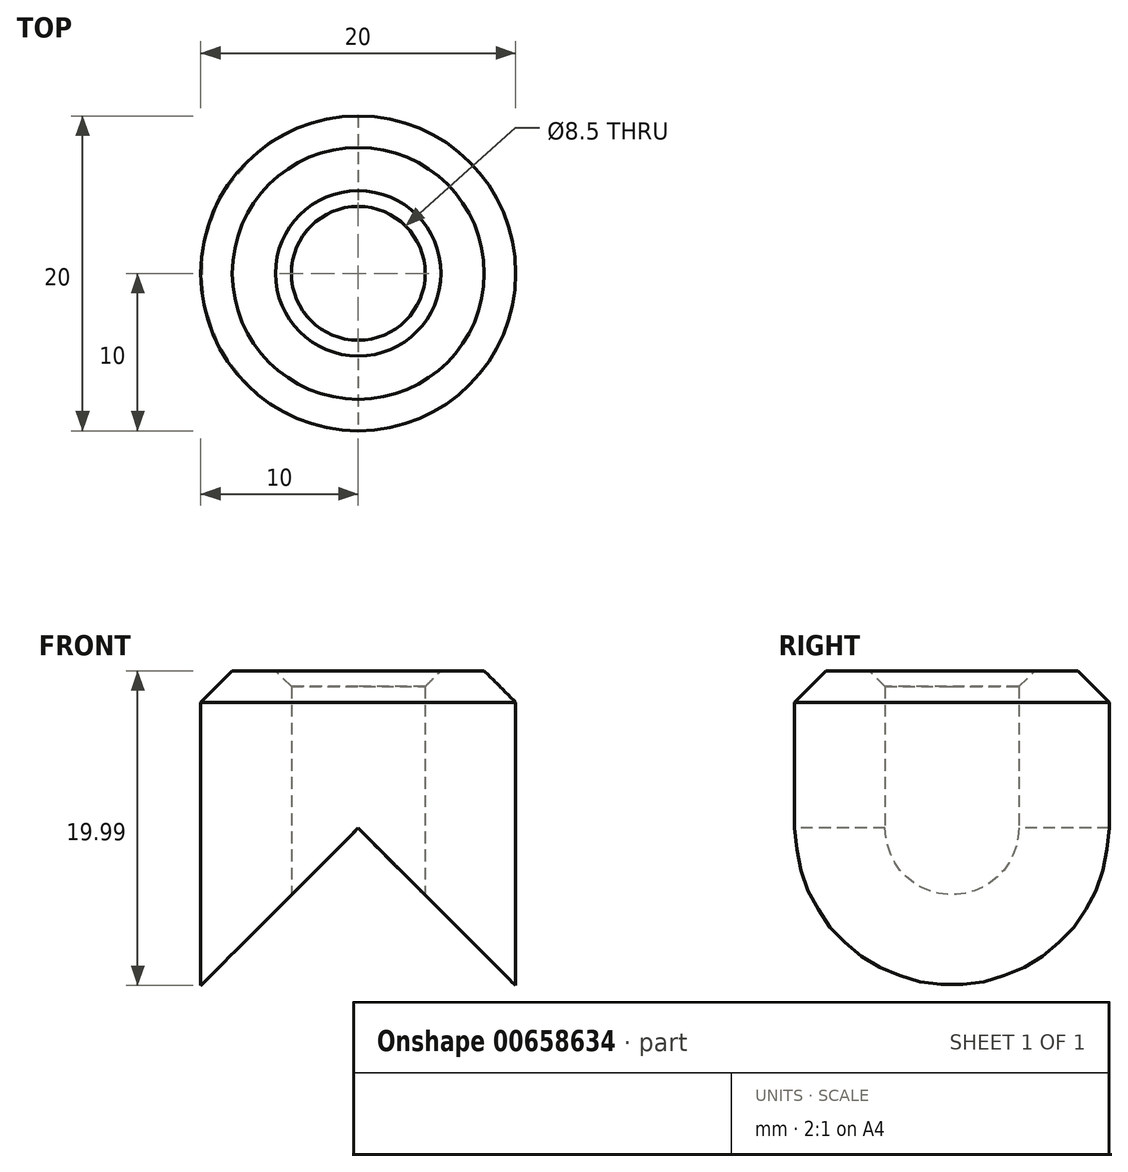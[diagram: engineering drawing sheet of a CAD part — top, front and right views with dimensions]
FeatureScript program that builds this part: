
annotation { "Feature Type Name" : "Feature", "Feature Type Description" : "" }
export const myFeature = defineFeature(function(context is Context, id is Id, definition is map)
    precondition{}
    {
        {
            var Q0;
            Q0=qCreatedBy(makeId("Top.planeOp"),FACE);
            var sketch = newSketch(context, id + "F0", { "sketchPlane" : qUnion([Q0])});
            skCircle(sketch, "E0", {"center": v(0, 0) * mm, "radius": 10 * mm});
            skCircle(sketch, "E1", {"center": v(0, 0) * mm, "radius": 4.25 * mm});
            skSolve(sketch);
        }
        {
            var Q0;
            Q0 = qSketchRegion(id + "F0", true);
            extrude(context, id + "F1", {"entities" : qUnion([Q0]), "depth" : 20 * mm, "offsetDistance" : 25 * mm});
        }
        {
            var Q0;
            Q0=qCreatedBy(makeId("Front.planeOp"),FACE);
            var sketch = newSketch(context, id + "F2", { "sketchPlane" : qUnion([Q0])});
            skLineSegment(sketch, "E2", {"start": v(-10.01, 0) * mm, "end": v(10.01, 0) * mm});
            skLineSegment(sketch, "E3", {"start": v(10.01, 0) * mm, "end": v(0, 10.01) * mm});
            skLineSegment(sketch, "E4", {"start": v(0, 10.01) * mm, "end": v(-10.01, 0) * mm});
            skSolve(sketch);
        }
        {
            var Q0;
            Q0 = qSketchRegion(id + "F2", true);
            extrude(context, id + "F3", {"entities" : qUnion([Q0]), "operationType" : NewBodyOperationType.REMOVE, "endBound" : BoundingType.SYMMETRIC, "oppositeDirection" : true, "depth" : 25 * mm, "offsetDistance" : 25 * mm});
        }
        {
            var Q0;
            Q0=makeQuery(id+"F1.opExtrude","CAP_EDGE",EDGE,{"disambiguationData":[OSD([sQuery(id+"F0.wireOp",EDGE,"E0")])],"isStart":false});
            chamfer(context, id + "F4", {"entities" : qUnion([Q0]), "width" : 2 * mm, "tangentPropagation" : true});
        }
        {
            var Q0;
            Q0=makeQuery(id+"F1.opExtrude","CAP_EDGE",EDGE,{"disambiguationData":[OSD([sQuery(id+"F0.wireOp",EDGE,"E1")])],"isStart":false});
            chamfer(context, id + "F5", {"entities" : qUnion([Q0]), "width" : 1 * mm, "tangentPropagation" : true});
        }
    });
